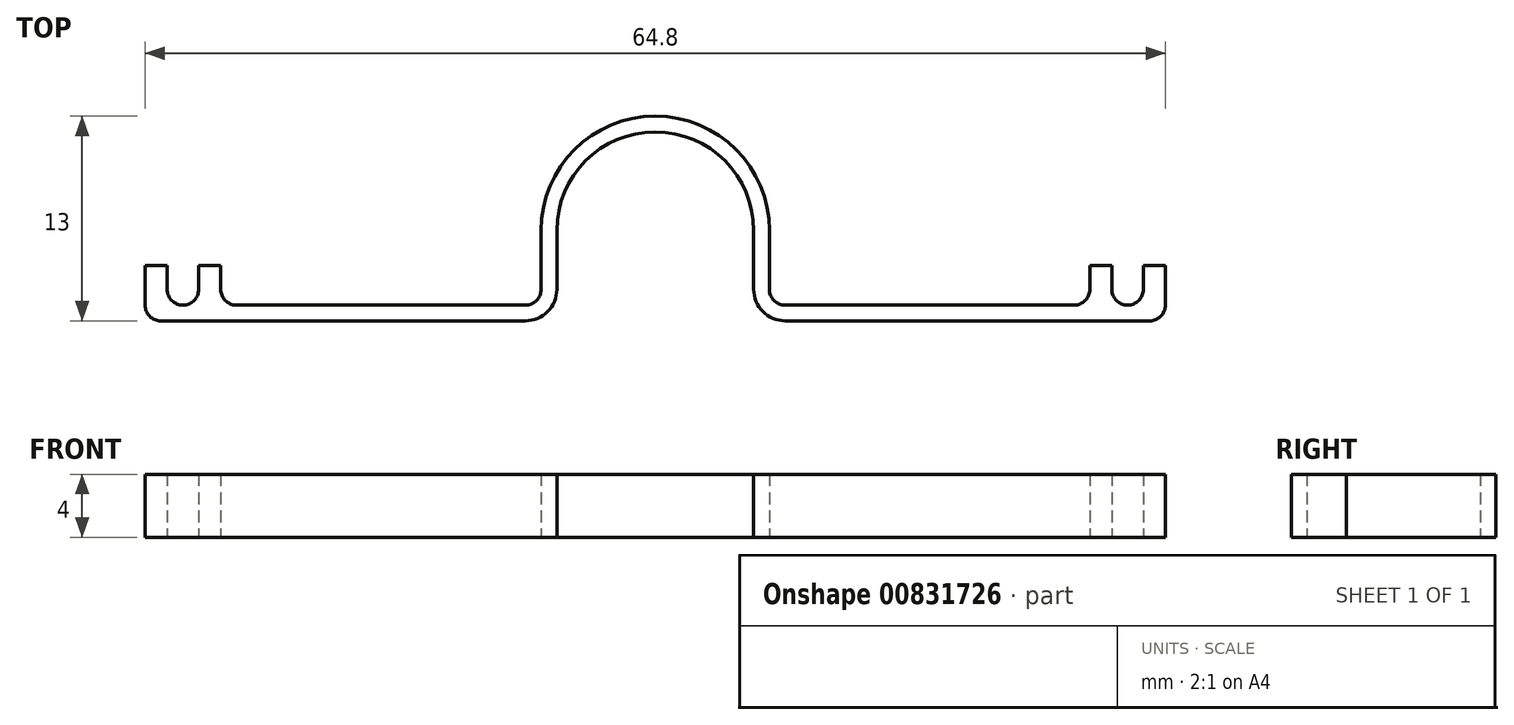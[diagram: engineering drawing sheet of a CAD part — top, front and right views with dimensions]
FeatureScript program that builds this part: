
annotation { "Feature Type Name" : "Feature", "Feature Type Description" : "" }
export const myFeature = defineFeature(function(context is Context, id is Id, definition is map)
    precondition{}
    {
        {
            var Q0;
            Q0=qCreatedBy(makeId("Top.planeOp"),FACE);
            var sketch = newSketch(context, id + "F0", { "sketchPlane" : qUnion([Q0])});
            skCircle(sketch, "E0", {"center": v(0, 0) * mm, "radius": 6.25 * mm});
            skLineSegment(sketch, "E1", {"start": v(-6.25, 0) * mm, "end": v(-6.25, -5.75) * mm});
            skLineSegment(sketch, "E2", {"start": v(-6.25, -5.75) * mm, "end": v(-32.4, -5.75) * mm});
            skLineSegment(sketch, "E3", {"start": v(-32.4, -5.75) * mm, "end": v(-32.4, -3.75) * mm});
            skLineSegment(sketch, "E4", {"start": v(-32.4, -3.75) * mm, "end": v(-31, -3.75) * mm});
            skArc(sketch, "E5", {"start": v(-31, -3.75) * mm, "mid": v(-30, -4.75) * mm, "end": v(-29, -3.75) * mm});
            skLineSegment(sketch, "E6", {"start": v(-29, -3.75) * mm, "end": v(-27.6, -3.75) * mm});
            skLineSegment(sketch, "E7", {"start": v(-27.6, -3.75) * mm, "end": v(-27.6, -4.75) * mm});
            skLineSegment(sketch, "E8", {"start": v(-27.6, -4.75) * mm, "end": v(-7.25, -4.75) * mm});
            skLineSegment(sketch, "E9", {"start": v(-7.25, -4.75) * mm, "end": v(-7.25, 0) * mm});
            skCircle(sketch, "E10", {"center": v(0, 0) * mm, "radius": 7.25 * mm});
            skLineSegment(sketch, "E11", {"start": v(0, 7.25) * mm, "end": v(0, 6.25) * mm});
            skCircle(sketch, "E12", {"center": v(-32.4, -4.75) * mm, "radius": 1 * mm});
            skSolve(sketch);
        }
        {
            var Q0;
            {var subQ2=sQuery(id+"F0.wireOp",EDGE,"E2");Q0=makeQuery(id+"F0.imprint","IMPRINT",FACE,{"disambiguationData":[TD([[makeQuery(id+"F0.imprint","IMPRINT",EDGE,{"derivedFrom":subQ2}),-1.0]])]});}
            var Q1;
            {var subQ0=sQuery(id+"F0.wireOp",EDGE,"E3");Q1=makeQuery(id+"F0.imprint","IMPRINT",FACE,{"disambiguationData":[TD([[makeQuery(id+"F0.imprint","IMPRINT",EDGE,{"derivedFrom":subQ0}),-1.0]])]});}
            var Q2;
            {var subQ0=sQuery(id+"F0.wireOp",EDGE,"E4");Q2=makeQuery(id+"F0.imprint","IMPRINT",FACE,{"disambiguationData":[TD([[makeQuery(id+"F0.imprint","IMPRINT",EDGE,{"derivedFrom":subQ0}),-1.0]])]});}
            var Q3;
            {var subQ2=sQuery(id+"F0.wireOp",EDGE,"E11");Q3=makeQuery(id+"F0.imprint","IMPRINT",FACE,{"disambiguationData":[TD([[makeQuery(id+"F0.imprint","IMPRINT",EDGE,{"derivedFrom":subQ2}),-1.0]])]});}
            extrude(context, id + "F1", {"entities" : qUnion([Q0, Q1, Q2, Q3]), "depth" : 4 * mm, "offsetDistance" : 25 * mm});
        }
        {
            var Q0;
            Q0=makeQuery(id+"F1.opExtrude","SWEPT_EDGE",EDGE,{"disambiguationData":[OSD([sQuery(id+"F0.wireOp",EDGE,"E7"),sQuery(id+"F0.wireOp",EDGE,"E8")])]});
            var Q1;
            Q1=makeQuery(id+"F1.opExtrude","SWEPT_EDGE",EDGE,{"disambiguationData":[OSD([sQuery(id+"F0.wireOp",EDGE,"E8"),sQuery(id+"F0.wireOp",EDGE,"E9")])]});
            fillet(context, id + "F2", {"entities" : qUnion([Q0, Q1]), "radius" : 1 * mm, "tangentPropagation" : true, "allowEdgeOverflow" : false});
        }
        {
            var Q0;
            Q0=makeQuery(id+"F1.opExtrude","SWEPT_EDGE",EDGE,{"disambiguationData":[OSD([sQuery(id+"F0.wireOp",EDGE,"E1"),sQuery(id+"F0.wireOp",EDGE,"E2")])]});
            fillet(context, id + "F3", {"entities" : qUnion([Q0]), "radius" : 2 * mm, "tangentPropagation" : true, "allowEdgeOverflow" : false});
        }
        {
            var Q0;
            Q0=makeQuery(id+"F1.opExtrude","SWEPT_FACE",FACE,{"disambiguationData":[OSD([sQuery(id+"F0.wireOp",EDGE,"E6")])]});
            var sketch = newSketch(context, id + "F4", { "sketchPlane" : qUnion([Q0])});
            skLineSegment(sketch, "E13.0.0", {"start": v(27.6, 0) * mm, "end": v(29, 0) * mm});
            skLineSegment(sketch, "E13.0.1", {"start": v(29, 0) * mm, "end": v(29, 4) * mm});
            skLineSegment(sketch, "E13.0.2", {"start": v(29, 4) * mm, "end": v(27.6, 4) * mm});
            skLineSegment(sketch, "E13.0.3", {"start": v(27.6, 4) * mm, "end": v(27.6, 0) * mm});
            skPoint(sketch, "E14.0", {"position": v(31.7, 4) * mm});
            skLineSegment(sketch, "E15.0.0", {"start": v(31, 0) * mm, "end": v(32.4, 0) * mm});
            skLineSegment(sketch, "E15.0.1", {"start": v(32.4, 0) * mm, "end": v(32.4, 4) * mm});
            skLineSegment(sketch, "E15.0.2", {"start": v(32.4, 4) * mm, "end": v(31, 4) * mm});
            skLineSegment(sketch, "E15.0.3", {"start": v(31, 4) * mm, "end": v(31, 0) * mm});
            skSolve(sketch);
        }
        {
            var Q0;
            Q0 = qSketchRegion(id + "F4", true);
            extrude(context, id + "F5", {"entities" : qUnion([Q0]), "operationType" : NewBodyOperationType.ADD, "depth" : 1.5 * mm, "offsetDistance" : 25 * mm});
        }
        {
            var Q0;
            Q0=makeQuery(id+"F1.opExtrude","SWEPT_EDGE",EDGE,{"disambiguationData":[OSD([sQuery(id+"F0.wireOp",EDGE,"E2"),sQuery(id+"F0.wireOp",EDGE,"E3"),sQuery(id+"F0.wireOp",EDGE,"E12")])]});
            fillet(context, id + "F6", {"entities" : qUnion([Q0]), "radius" : 1 * mm, "tangentPropagation" : true, "allowEdgeOverflow" : false});
        }
        {
            var Q0;
            Q0=makeQuery(id+"F1.opExtrude","SWEPT_BODY",BODY,{"disambiguationData":[OSD([sQuery(id+"F0.wireOp",EDGE,"E0"),sQuery(id+"F0.wireOp",EDGE,"E1"),sQuery(id+"F0.wireOp",EDGE,"E2"),sQuery(id+"F0.wireOp",EDGE,"E4"),sQuery(id+"F0.wireOp",EDGE,"E5"),sQuery(id+"F0.wireOp",EDGE,"E6"),sQuery(id+"F0.wireOp",EDGE,"E7"),sQuery(id+"F0.wireOp",EDGE,"E8"),sQuery(id+"F0.wireOp",EDGE,"E9"),sQuery(id+"F0.wireOp",EDGE,"E10"),sQuery(id+"F0.wireOp",EDGE,"E11"),sQuery(id+"F0.wireOp",EDGE,"E12")])]});
            var Q1;
            Q1=qCreatedBy(makeId("Right.planeOp"),FACE);
            mirror(context, id + "F7", {"operationType" : NewBodyOperationType.ADD, "entities" : qUnion([Q0]), "mirrorPlane" : qUnion([Q1])});
        }
    });
